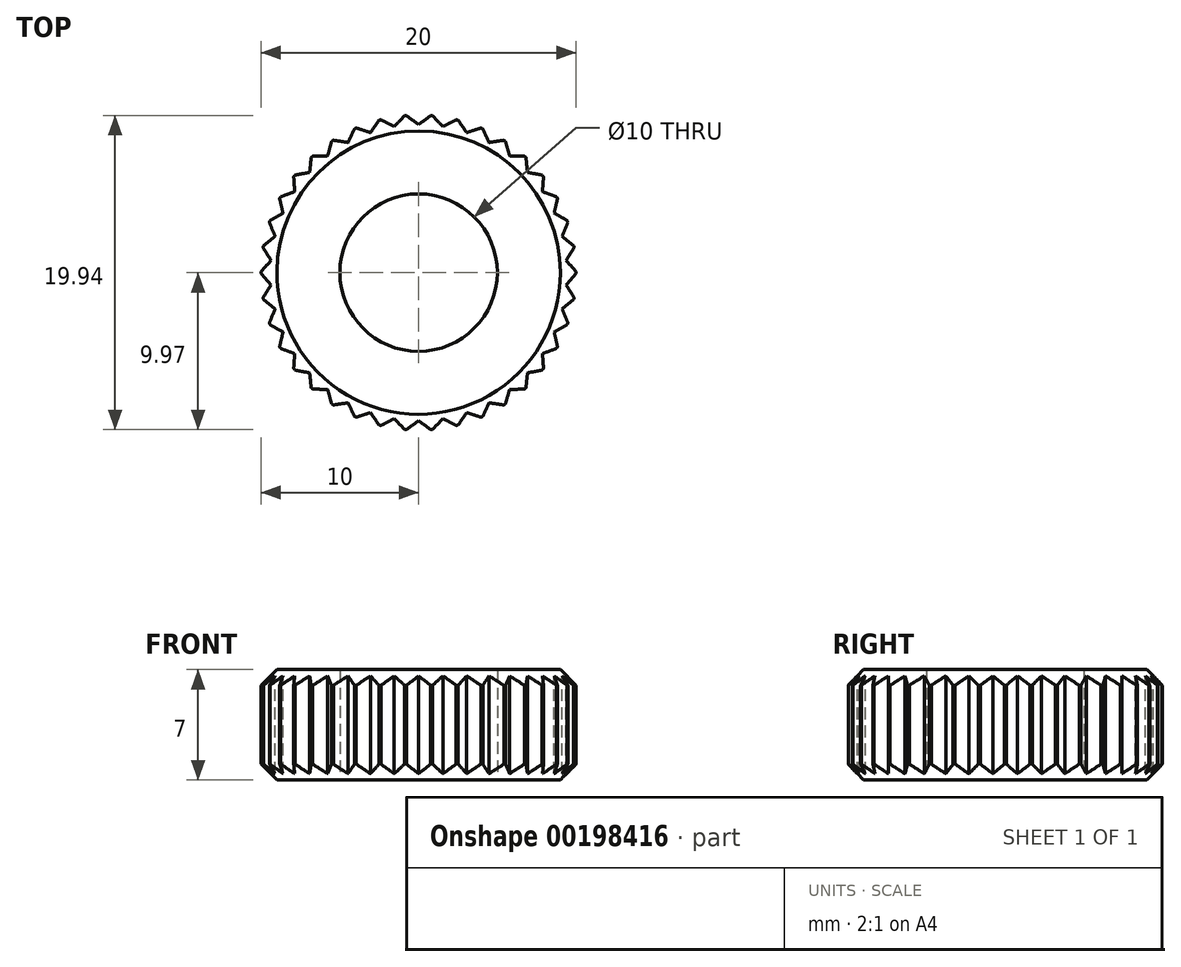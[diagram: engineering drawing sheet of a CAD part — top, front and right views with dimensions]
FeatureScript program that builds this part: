
annotation { "Feature Type Name" : "Feature", "Feature Type Description" : "" }
export const myFeature = defineFeature(function(context is Context, id is Id, definition is map)
    precondition{}
    {
        {
            var Q0;
            Q0=qCreatedBy(makeId("Top.planeOp"),FACE);
            var sketch = newSketch(context, id + "F0", { "sketchPlane" : qUnion([Q0])});
            skCircle(sketch, "E0", {"center": v(0, 0) * mm, "radius": 5 * mm});
            skCircle(sketch, "E1", {"center": v(0, 0) * mm, "radius": 10 * mm});
            skSolve(sketch);
        }
        {
            var Q0;
            Q0=makeQuery(id+"F0.imprint","IMPRINT",FACE,{"disambiguationData":[TD([[makeQuery(id+"F0.imprint","IMPRINT",EDGE,{"derivedFrom":sQuery(id+"F0.wireOp",EDGE,"E0")}),-1.0]])]});
            extrude(context, id + "F1", {"entities" : qUnion([Q0]), "depth" : 7 * mm});
        }
        {
            var Q0;
            Q0=makeQuery(id+"F1.opExtrude","CAP_EDGE",EDGE,{"disambiguationData":[OSD([sQuery(id+"F0.wireOp",EDGE,"E1")])],"isStart":false});
            var Q1;
            Q1=makeQuery(id+"F1.opExtrude","CAP_EDGE",EDGE,{"disambiguationData":[OSD([sQuery(id+"F0.wireOp",EDGE,"E1")])],"isStart":true});
            chamfer(context, id + "F2", {"entities" : qUnion([Q0, Q1]), "width" : 1 * mm, "tangentPropagation" : true});
        }
        {
            var Q0;
            Q0=qCreatedBy(makeId("Top.planeOp"),FACE);
            var sketch = newSketch(context, id + "F3", { "sketchPlane" : qUnion([Q0])});
            skLineSegment(sketch, "E2", {"start": v(0, 9.4) * mm, "end": v(-0.83, 10.02) * mm});
            skLineSegment(sketch, "E3.MirrorCS", {"start": v(0, 9.4) * mm, "end": v(0.83, 10.02) * mm});
            skLineSegment(sketch, "E4.1.0", {"start": v(-1.55, 9.27) * mm, "end": v(-0.83, 10.02) * mm});
            skLineSegment(sketch, "E4.1.1", {"start": v(-1.55, 9.27) * mm, "end": v(-2.47, 9.75) * mm});
            skLineSegment(sketch, "E4.2.0", {"start": v(-3.05, 8.9) * mm, "end": v(-2.47, 9.75) * mm});
            skLineSegment(sketch, "E4.2.1", {"start": v(-3.05, 8.9) * mm, "end": v(-4.04, 9.21) * mm});
            skLineSegment(sketch, "E4.3.0", {"start": v(-4.47, 8.27) * mm, "end": v(-4.04, 9.21) * mm});
            skLineSegment(sketch, "E4.3.1", {"start": v(-4.47, 8.27) * mm, "end": v(-5.5, 8.42) * mm});
            skLineSegment(sketch, "E4.4.0", {"start": v(-5.77, 7.42) * mm, "end": v(-5.5, 8.42) * mm});
            skLineSegment(sketch, "E4.4.1", {"start": v(-5.77, 7.42) * mm, "end": v(-6.81, 7.4) * mm});
            skLineSegment(sketch, "E4.5.0", {"start": v(-6.92, 6.37) * mm, "end": v(-6.81, 7.4) * mm});
            skLineSegment(sketch, "E4.5.1", {"start": v(-6.92, 6.37) * mm, "end": v(-7.94, 6.18) * mm});
            skLineSegment(sketch, "E4.6.0", {"start": v(-7.87, 5.14) * mm, "end": v(-7.94, 6.18) * mm});
            skLineSegment(sketch, "E4.6.1", {"start": v(-7.87, 5.14) * mm, "end": v(-8.85, 4.79) * mm});
            skLineSegment(sketch, "E4.7.0", {"start": v(-8.6, 3.78) * mm, "end": v(-8.85, 4.79) * mm});
            skLineSegment(sketch, "E4.7.1", {"start": v(-8.6, 3.78) * mm, "end": v(-9.51, 3.27) * mm});
            skLineSegment(sketch, "E4.8.0", {"start": v(-9.11, 2.3) * mm, "end": v(-9.51, 3.27) * mm});
            skLineSegment(sketch, "E4.8.1", {"start": v(-9.11, 2.3) * mm, "end": v(-9.92, 1.66) * mm});
            skLineSegment(sketch, "E4.9.0", {"start": v(-9.37, 0.78) * mm, "end": v(-9.92, 1.66) * mm});
            skLineSegment(sketch, "E4.9.1", {"start": v(-9.37, 0.78) * mm, "end": v(-10.06, 0) * mm});
            skLineSegment(sketch, "E4.10.0", {"start": v(-9.37, -0.78) * mm, "end": v(-10.06, 0) * mm});
            skLineSegment(sketch, "E4.10.1", {"start": v(-9.37, -0.78) * mm, "end": v(-9.92, -1.66) * mm});
            skLineSegment(sketch, "E4.11.0", {"start": v(-9.11, -2.3) * mm, "end": v(-9.92, -1.66) * mm});
            skLineSegment(sketch, "E4.11.1", {"start": v(-9.11, -2.3) * mm, "end": v(-9.51, -3.27) * mm});
            skLineSegment(sketch, "E4.12.0", {"start": v(-8.6, -3.78) * mm, "end": v(-9.51, -3.27) * mm});
            skLineSegment(sketch, "E4.12.1", {"start": v(-8.6, -3.78) * mm, "end": v(-8.85, -4.79) * mm});
            skLineSegment(sketch, "E4.13.0", {"start": v(-7.87, -5.14) * mm, "end": v(-8.85, -4.79) * mm});
            skLineSegment(sketch, "E4.13.1", {"start": v(-7.87, -5.14) * mm, "end": v(-7.94, -6.18) * mm});
            skLineSegment(sketch, "E4.14.0", {"start": v(-6.92, -6.37) * mm, "end": v(-7.94, -6.18) * mm});
            skLineSegment(sketch, "E4.14.1", {"start": v(-6.92, -6.37) * mm, "end": v(-6.81, -7.4) * mm});
            skLineSegment(sketch, "E4.15.0", {"start": v(-5.77, -7.42) * mm, "end": v(-6.81, -7.4) * mm});
            skLineSegment(sketch, "E4.15.1", {"start": v(-5.77, -7.42) * mm, "end": v(-5.5, -8.42) * mm});
            skLineSegment(sketch, "E4.16.0", {"start": v(-4.47, -8.27) * mm, "end": v(-5.5, -8.42) * mm});
            skLineSegment(sketch, "E4.16.1", {"start": v(-4.47, -8.27) * mm, "end": v(-4.04, -9.21) * mm});
            skLineSegment(sketch, "E4.17.0", {"start": v(-3.05, -8.9) * mm, "end": v(-4.04, -9.21) * mm});
            skLineSegment(sketch, "E4.17.1", {"start": v(-3.05, -8.9) * mm, "end": v(-2.47, -9.75) * mm});
            skLineSegment(sketch, "E4.18.0", {"start": v(-1.55, -9.27) * mm, "end": v(-2.47, -9.75) * mm});
            skLineSegment(sketch, "E4.18.1", {"start": v(-1.55, -9.27) * mm, "end": v(-0.83, -10.02) * mm});
            skLineSegment(sketch, "E4.19.0", {"start": v(0, -9.4) * mm, "end": v(-0.83, -10.02) * mm});
            skLineSegment(sketch, "E4.19.1", {"start": v(0, -9.4) * mm, "end": v(0.83, -10.02) * mm});
            skLineSegment(sketch, "E4.20.0", {"start": v(1.55, -9.27) * mm, "end": v(0.83, -10.02) * mm});
            skLineSegment(sketch, "E4.20.1", {"start": v(1.55, -9.27) * mm, "end": v(2.47, -9.75) * mm});
            skLineSegment(sketch, "E4.21.0", {"start": v(3.05, -8.9) * mm, "end": v(2.47, -9.75) * mm});
            skLineSegment(sketch, "E4.21.1", {"start": v(3.05, -8.9) * mm, "end": v(4.04, -9.21) * mm});
            skLineSegment(sketch, "E4.22.0", {"start": v(4.47, -8.27) * mm, "end": v(4.04, -9.21) * mm});
            skLineSegment(sketch, "E4.22.1", {"start": v(4.47, -8.27) * mm, "end": v(5.5, -8.42) * mm});
            skLineSegment(sketch, "E4.23.0", {"start": v(5.77, -7.42) * mm, "end": v(5.5, -8.42) * mm});
            skLineSegment(sketch, "E4.23.1", {"start": v(5.77, -7.42) * mm, "end": v(6.81, -7.4) * mm});
            skLineSegment(sketch, "E4.24.0", {"start": v(6.92, -6.37) * mm, "end": v(6.81, -7.4) * mm});
            skLineSegment(sketch, "E4.24.1", {"start": v(6.92, -6.37) * mm, "end": v(7.94, -6.18) * mm});
            skLineSegment(sketch, "E4.25.0", {"start": v(7.87, -5.14) * mm, "end": v(7.94, -6.18) * mm});
            skLineSegment(sketch, "E4.25.1", {"start": v(7.87, -5.14) * mm, "end": v(8.85, -4.79) * mm});
            skLineSegment(sketch, "E4.26.0", {"start": v(8.6, -3.78) * mm, "end": v(8.85, -4.79) * mm});
            skLineSegment(sketch, "E4.26.1", {"start": v(8.6, -3.78) * mm, "end": v(9.51, -3.27) * mm});
            skLineSegment(sketch, "E4.27.0", {"start": v(9.11, -2.3) * mm, "end": v(9.51, -3.27) * mm});
            skLineSegment(sketch, "E4.27.1", {"start": v(9.11, -2.3) * mm, "end": v(9.92, -1.66) * mm});
            skLineSegment(sketch, "E4.28.0", {"start": v(9.37, -0.78) * mm, "end": v(9.92, -1.66) * mm});
            skLineSegment(sketch, "E4.28.1", {"start": v(9.37, -0.78) * mm, "end": v(10.06, 0) * mm});
            skLineSegment(sketch, "E4.29.0", {"start": v(9.37, 0.78) * mm, "end": v(10.06, 0) * mm});
            skLineSegment(sketch, "E4.29.1", {"start": v(9.37, 0.78) * mm, "end": v(9.92, 1.66) * mm});
            skLineSegment(sketch, "E4.30.0", {"start": v(9.11, 2.3) * mm, "end": v(9.92, 1.66) * mm});
            skLineSegment(sketch, "E4.30.1", {"start": v(9.11, 2.3) * mm, "end": v(9.51, 3.27) * mm});
            skLineSegment(sketch, "E4.31.0", {"start": v(8.6, 3.78) * mm, "end": v(9.51, 3.27) * mm});
            skLineSegment(sketch, "E4.31.1", {"start": v(8.6, 3.78) * mm, "end": v(8.85, 4.79) * mm});
            skLineSegment(sketch, "E4.32.0", {"start": v(7.87, 5.14) * mm, "end": v(8.85, 4.79) * mm});
            skLineSegment(sketch, "E4.32.1", {"start": v(7.87, 5.14) * mm, "end": v(7.94, 6.18) * mm});
            skLineSegment(sketch, "E4.33.0", {"start": v(6.92, 6.37) * mm, "end": v(7.94, 6.18) * mm});
            skLineSegment(sketch, "E4.33.1", {"start": v(6.92, 6.37) * mm, "end": v(6.81, 7.4) * mm});
            skLineSegment(sketch, "E4.34.0", {"start": v(5.77, 7.42) * mm, "end": v(6.81, 7.4) * mm});
            skLineSegment(sketch, "E4.34.1", {"start": v(5.77, 7.42) * mm, "end": v(5.5, 8.42) * mm});
            skLineSegment(sketch, "E4.35.0", {"start": v(4.47, 8.27) * mm, "end": v(5.5, 8.42) * mm});
            skLineSegment(sketch, "E4.35.1", {"start": v(4.47, 8.27) * mm, "end": v(4.04, 9.21) * mm});
            skLineSegment(sketch, "E4.36.0", {"start": v(3.05, 8.9) * mm, "end": v(4.04, 9.21) * mm});
            skLineSegment(sketch, "E4.36.1", {"start": v(3.05, 8.9) * mm, "end": v(2.47, 9.75) * mm});
            skLineSegment(sketch, "E4.37.0", {"start": v(1.55, 9.27) * mm, "end": v(2.47, 9.75) * mm});
            skLineSegment(sketch, "E4.37.1", {"start": v(1.55, 9.27) * mm, "end": v(0.83, 10.02) * mm});
            skPoint(sketch, "E4.center", {"position": v(0, 0) * mm});
            skLineSegment(sketch, "E5.trimOffspring", {"start": v(2.94, 11.6) * mm, "end": v(2.9, 11.67) * mm});
            skPoint(sketch, "E6.orphan", {"position": v(6.54, 10.1) * mm});
            skPoint(sketch, "E7.orphan", {"position": v(-3, -11.65) * mm});
            skPoint(sketch, "E8.orphan", {"position": v(-2.9, -11.67) * mm});
            skLineSegment(sketch, "E9.trimOffspring", {"start": v(-0.99, 11.93) * mm, "end": v(-1.04, 11.98) * mm});
            skLineSegment(sketch, "E10.trimOffspring", {"start": v(-0.99, 11.93) * mm, "end": v(-0.95, 11.99) * mm});
            skPoint(sketch, "E11.trimOffspring.end.orphan", {"position": v(-3, 11.65) * mm});
            skLineSegment(sketch, "E12.trimOffspring", {"start": v(0.99, 11.93) * mm, "end": v(1.04, 11.98) * mm});
            skPoint(sketch, "E13.trimOffspring.end.orphan", {"position": v(3, 11.65) * mm});
            skCircle(sketch, "E14", {"center": v(0, 0) * mm, "radius": 11.31 * mm});
            skSolve(sketch);
        }
        {
            var Q0;
            Q0=makeQuery(id+"F3.imprint","IMPRINT",FACE,{"disambiguationData":[TD([[makeQuery(id+"F3.imprint","IMPRINT",EDGE,{"derivedFrom":sQuery(id+"F3.wireOp",EDGE,"E2")}),-1.0]])]});
            extrude(context, id + "F4", {"entities" : qUnion([Q0]), "operationType" : NewBodyOperationType.REMOVE, "oppositeDirection" : true, "depth" : 25 * mm, "hasSecondDirection" : true, "secondDirectionOppositeDirection" : false, "secondDirectionDepth" : 25 * mm});
        }
    });
